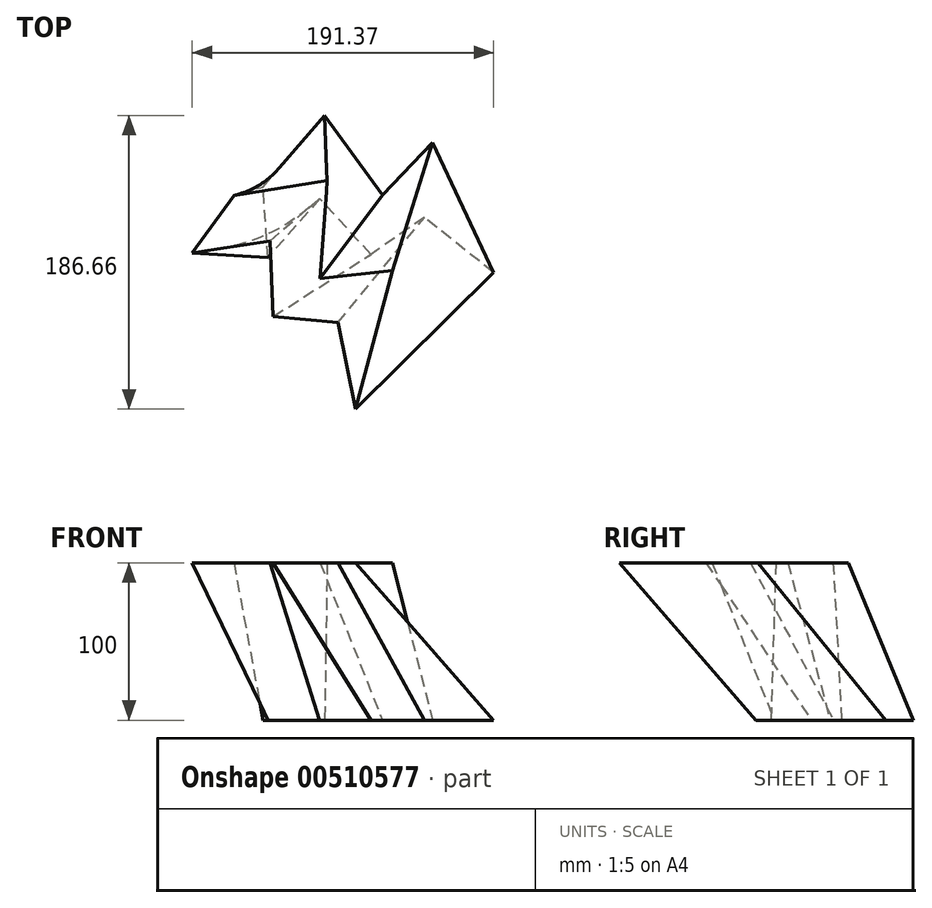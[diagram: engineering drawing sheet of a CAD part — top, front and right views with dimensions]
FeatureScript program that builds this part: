
annotation { "Feature Type Name" : "Feature", "Feature Type Description" : "" }
export const myFeature = defineFeature(function(context is Context, id is Id, definition is map)
    precondition{}
    {
        {
            var Q0;
            Q0=qCreatedBy(makeId("Top.planeOp"),FACE);
            var sketch = newSketch(context, id + "F0", { "sketchPlane" : qUnion([Q0])});
            skLineSegment(sketch, "E0", {"start": v(-47.55, 5.08) * mm, "end": v(-8.34, 50.56) * mm});
            skLineSegment(sketch, "E1", {"start": v(-8.34, 50.56) * mm, "end": v(28.25, 0) * mm});
            skLineSegment(sketch, "E2", {"start": v(28.25, 0) * mm, "end": v(60.14, 33.3) * mm});
            skLineSegment(sketch, "E3", {"start": v(60.14, 33.3) * mm, "end": v(98.82, -49.29) * mm});
            skLineSegment(sketch, "E4", {"start": v(98.82, -49.29) * mm, "end": v(54.9, -14.26) * mm});
            skLineSegment(sketch, "E5", {"start": v(54.9, -14.26) * mm, "end": v(20.93, -37.78) * mm});
            skLineSegment(sketch, "E6", {"start": v(20.93, -37.78) * mm, "end": v(-11.48, -2.24) * mm});
            skLineSegment(sketch, "E7", {"start": v(-11.48, -2.24) * mm, "end": v(-44.41, -39.88) * mm});
            skLineSegment(sketch, "E8", {"start": v(-44.41, -39.88) * mm, "end": v(-47.55, 5.08) * mm});
            skSolve(sketch);
        }
        {
            var Q0;
            Q0=qCreatedBy(makeId("Top.planeOp"),FACE);
            cPlane(context, id + "F1", {"entities" : qUnion([Q0]), "cplaneType" : CPlaneType.OFFSET, "offset" : 100 * mm, "width" : 150 * mm, "height" : 150 * mm});
        }
        {
            var Q0;
            Q0=qCreatedBy(id+"F1.planeOp",FACE);
            var sketch = newSketch(context, id + "F2", { "sketchPlane" : qUnion([Q0])});
            skLineSegment(sketch, "E9", {"start": v(-66.06, -0.37) * mm, "end": v(-6.79, 9.27) * mm});
            skLineSegment(sketch, "E10", {"start": v(-6.79, 9.27) * mm, "end": v(-11.26, -52.98) * mm});
            skLineSegment(sketch, "E11", {"start": v(-11.26, -52.98) * mm, "end": v(34.58, -47.96) * mm});
            skLineSegment(sketch, "E12", {"start": v(34.58, -47.96) * mm, "end": v(11.12, -136.1) * mm});
            skLineSegment(sketch, "E13", {"start": v(11.12, -136.1) * mm, "end": v(0, -81.04) * mm});
            skLineSegment(sketch, "E14", {"start": v(0, -81.04) * mm, "end": v(-41.15, -77.22) * mm});
            skLineSegment(sketch, "E15", {"start": v(-41.15, -77.22) * mm, "end": v(-43.13, -29.16) * mm});
            skLineSegment(sketch, "E16", {"start": v(-43.13, -29.16) * mm, "end": v(-92.55, -36.82) * mm});
            skLineSegment(sketch, "E17", {"start": v(-92.55, -36.82) * mm, "end": v(-66.06, -0.37) * mm});
            skSolve(sketch);
        }
        {
            var Q0;
            Q0=makeQuery(id+"F2.imprint","IMPRINT",FACE,{"disambiguationData":[TD([[makeQuery(id+"F2.imprint","IMPRINT",EDGE,{"derivedFrom":sQuery(id+"F2.wireOp",EDGE,"E9")}),-1.0]])]});
            var Q1;
            Q1=makeQuery(id+"F0.imprint","IMPRINT",FACE,{"disambiguationData":[TD([[makeQuery(id+"F0.imprint","IMPRINT",EDGE,{"derivedFrom":sQuery(id+"F0.wireOp",EDGE,"E0")}),-1.0]])]});
            loft(context, id + "F3", {"sheetProfilesArray" : [{ "sheetProfileEntities" : qUnion([Q0]) }, { "sheetProfileEntities" : qUnion([Q1]) }]});
        }
    });
